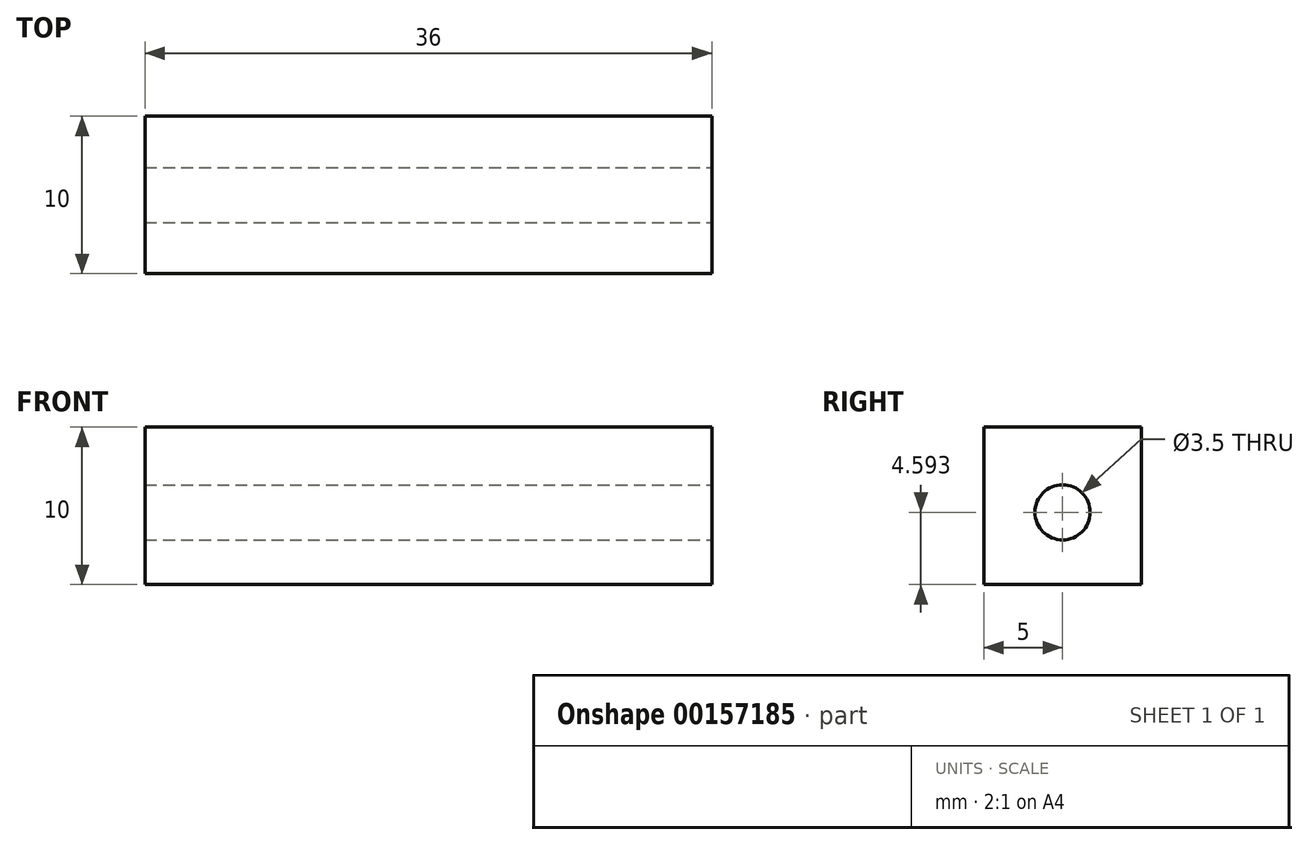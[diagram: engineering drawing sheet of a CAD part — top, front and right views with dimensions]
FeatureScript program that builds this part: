
annotation { "Feature Type Name" : "Feature", "Feature Type Description" : "" }
export const myFeature = defineFeature(function(context is Context, id is Id, definition is map)
    precondition{}
    {
        {
            var Q0;
            Q0=qCreatedBy(makeId("Top.planeOp"),FACE);
            var sketch = newSketch(context, id + "F0", { "sketchPlane" : qUnion([Q0])});
            skLineSegment(sketch, "E0.bottom", {"start": v(-18, 5) * mm, "end": v(18, 5) * mm});
            skLineSegment(sketch, "E0.top", {"start": v(-18, -5) * mm, "end": v(18, -5) * mm});
            skLineSegment(sketch, "E0.left", {"start": v(-18, 5) * mm, "end": v(-18, -5) * mm});
            skLineSegment(sketch, "E0.right", {"start": v(18, 5) * mm, "end": v(18, -5) * mm});
            skPoint(sketch, "E0.middle", {"position": v(0, 0) * mm});
            skSolve(sketch);
        }
        {
            var Q0;
            Q0 = qSketchRegion(id + "F0", true);
            extrude(context, id + "F1", {"entities" : qUnion([Q0]), "depth" : 10 * mm});
        }
        {
            var Q0;
            Q0=makeQuery(id+"F1.opExtrude","SWEPT_FACE",FACE,{"disambiguationData":[OSD([sQuery(id+"F0.wireOp",EDGE,"E0.right")])]});
            var sketch = newSketch(context, id + "F2", { "sketchPlane" : qUnion([Q0])});
            skCircle(sketch, "E1", {"center": v(0, 4.6) * mm, "radius": 1.75 * mm});
            skSolve(sketch);
        }
        {
            var Q0;
            Q0 = qSketchRegion(id + "F2", true);
            extrude(context, id + "F3", {"entities" : qUnion([Q0]), "operationType" : NewBodyOperationType.REMOVE, "oppositeDirection" : true, "depth" : 36 * mm});
        }
    });
